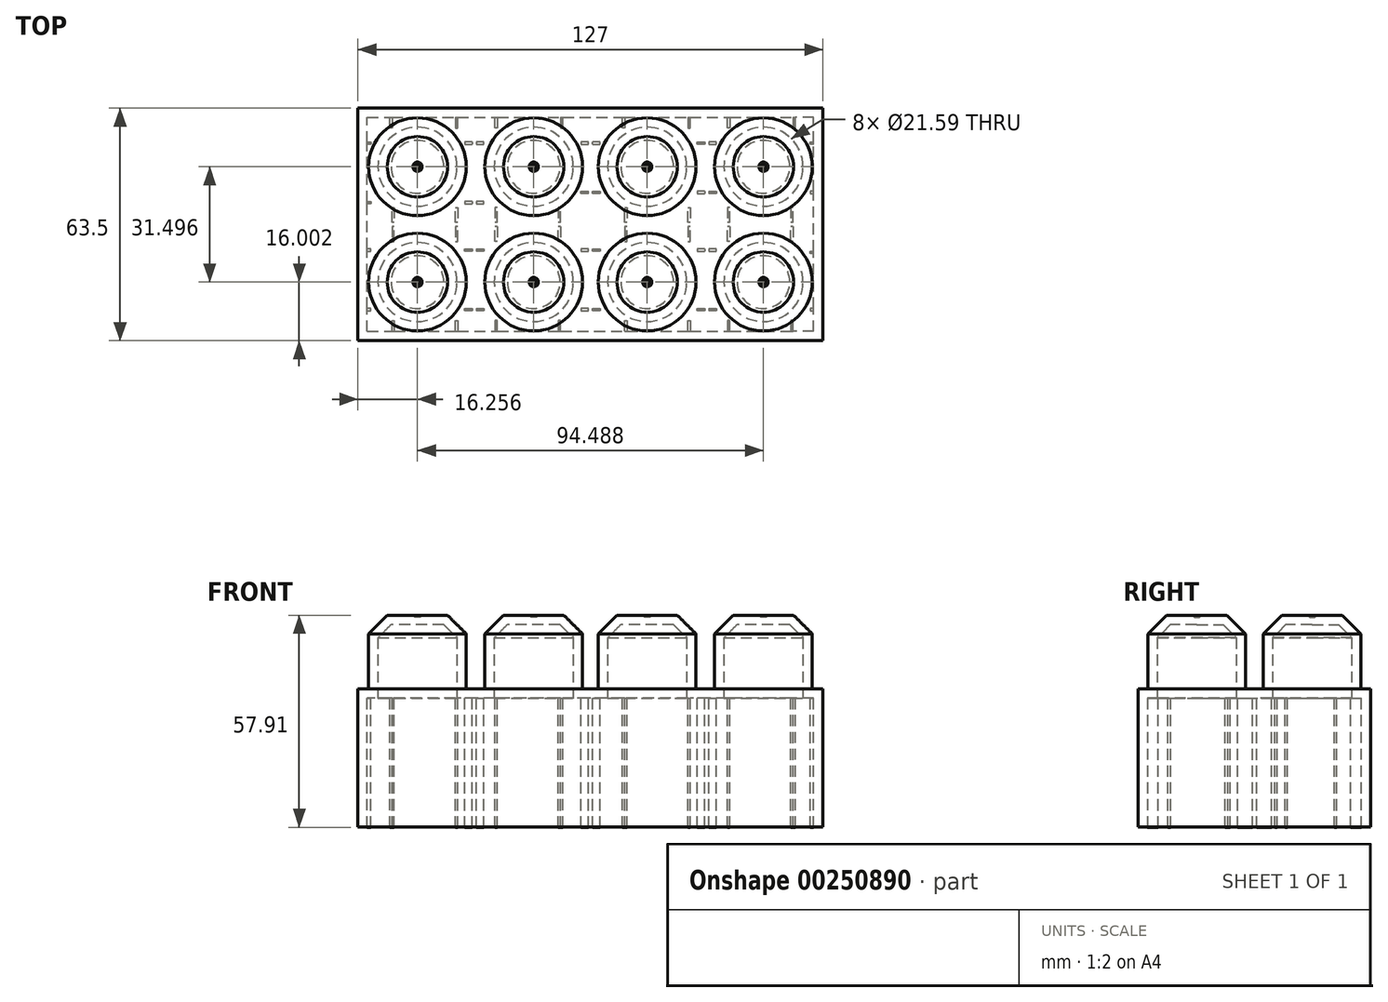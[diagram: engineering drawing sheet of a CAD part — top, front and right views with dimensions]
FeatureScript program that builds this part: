
annotation { "Feature Type Name" : "Feature", "Feature Type Description" : "" }
export const myFeature = defineFeature(function(context is Context, id is Id, definition is map)
    precondition{}
    {
        {
            var Q0;
            Q0=qCreatedBy(makeId("Front.planeOp"),FACE);
            var sketch = newSketch(context, id + "F0", { "sketchPlane" : qUnion([Q0])});
            skLineSegment(sketch, "E0", {"start": v(0, 0) * mm, "end": v(127, 0) * mm});
            skLineSegment(sketch, "E1", {"start": v(127, 0) * mm, "end": v(127, 37.74) * mm});
            skLineSegment(sketch, "E2", {"start": v(127, 37.74) * mm, "end": v(0, 37.74) * mm});
            skLineSegment(sketch, "E3", {"start": v(0, 37.74) * mm, "end": v(0, 0) * mm});
            skSolve(sketch);
        }
        {
            var Q0;
            Q0=makeQuery(id+"F0.imprint","IMPRINT",FACE,{"disambiguationData":[TD([[makeQuery(id+"F0.imprint","IMPRINT",EDGE,{"derivedFrom":sQuery(id+"F0.wireOp",EDGE,"E0")}),1.0]])]});
            extrude(context, id + "F1", {"entities" : qUnion([Q0]), "depth" : 63.5 * mm});
        }
        {
            var Q0;
            Q0=makeQuery(id+"F1.opExtrude","SWEPT_FACE",FACE,{"disambiguationData":[OSD([sQuery(id+"F0.wireOp",EDGE,"E2")])]});
            var sketch = newSketch(context, id + "F2", { "sketchPlane" : qUnion([Q0])});
            skLineSegment(sketch, "E4", {"start": v(0, -63.5) * mm, "end": v(16.26, -63.5) * mm});
            skLineSegment(sketch, "E5", {"start": v(16.26, -63.5) * mm, "end": v(16.26, -47.5) * mm});
            skCircle(sketch, "E6", {"center": v(16.26, -47.5) * mm, "radius": 13.34 * mm});
            skCircle(sketch, "E7", {"center": v(16.26, -16) * mm, "radius": 13.34 * mm});
            skLineSegment(sketch, "E8", {"start": v(0, -63.5) * mm, "end": v(48, -63.5) * mm});
            skCircle(sketch, "E9", {"center": v(48, -47.5) * mm, "radius": 13.34 * mm});
            skCircle(sketch, "E10", {"center": v(48, -16) * mm, "radius": 13.34 * mm});
            skCircle(sketch, "E11", {"center": v(110.74, -16) * mm, "radius": 13.34 * mm});
            skCircle(sketch, "E12", {"center": v(79, -16) * mm, "radius": 13.34 * mm});
            skCircle(sketch, "E13", {"center": v(79, -47.5) * mm, "radius": 13.34 * mm});
            skCircle(sketch, "E14", {"center": v(110.74, -47.5) * mm, "radius": 13.34 * mm});
            skSolve(sketch);
        }
        {
            var Q0;
            Q0 = qSketchRegion(id + "F2", true);
            extrude(context, id + "F3", {"entities" : qUnion([Q0]), "operationType" : NewBodyOperationType.ADD, "depth" : 20.1 * mm});
        }
        {
            var Q0;
            Q0=makeQuery(id+"F3.opExtrude","CAP_FACE",FACE,{"disambiguationData":[OSD([sQuery(id+"F2.wireOp",EDGE,"E6")])],"isStart":false});
            var Q1;
            Q1=makeQuery(id+"F3.opExtrude","CAP_EDGE",EDGE,{"disambiguationData":[OSD([sQuery(id+"F2.wireOp",EDGE,"E7")])],"isStart":false});
            var Q2;
            Q2=makeQuery(id+"F3.opExtrude","CAP_EDGE",EDGE,{"disambiguationData":[OSD([sQuery(id+"F2.wireOp",EDGE,"E10")])],"isStart":false});
            var Q3;
            Q3=makeQuery(id+"F3.opExtrude","CAP_FACE",FACE,{"disambiguationData":[OSD([sQuery(id+"F2.wireOp",EDGE,"E12")])],"isStart":false});
            var Q4;
            Q4=makeQuery(id+"F3.opExtrude","CAP_FACE",FACE,{"disambiguationData":[OSD([sQuery(id+"F2.wireOp",EDGE,"E9")])],"isStart":false});
            var Q5;
            Q5=makeQuery(id+"F3.opExtrude","CAP_FACE",FACE,{"disambiguationData":[OSD([sQuery(id+"F2.wireOp",EDGE,"E14")])],"isStart":false});
            var Q6;
            Q6=makeQuery(id+"F3.opExtrude","CAP_FACE",FACE,{"disambiguationData":[OSD([sQuery(id+"F2.wireOp",EDGE,"E11")])],"isStart":false});
            var Q7;
            Q7=makeQuery(id+"F3.opExtrude","CAP_FACE",FACE,{"disambiguationData":[OSD([sQuery(id+"F2.wireOp",EDGE,"E13")])],"isStart":false});
            chamfer(context, id + "F4", {"entities" : qUnion([Q0, Q1, Q2, Q3, Q4, Q5, Q6, Q7]), "width" : 5.08 * mm, "tangentPropagation" : true});
        }
        {
            var Q0;
            Q0=makeQuery(id+"F1.opExtrude","SWEPT_FACE",FACE,{"disambiguationData":[OSD([sQuery(id+"F0.wireOp",EDGE,"E0")])]});
            shell(context, id + "F5", {"entities" : qUnion([Q0]), "thickness" : 2.54 * mm});
        }
        {
            var Q0;
            Q0=makeQuery(id+"F5.opShell","OFFSET_FACE",FACE,{"disambiguationData":[OSD([sQuery(id+"F0.wireOp",EDGE,"E2")])]});
            var sketch = newSketch(context, id + "F6", { "sketchPlane" : qUnion([Q0])});
            skLineSegment(sketch, "E15.bottom", {"start": v(125.58, 62.08) * mm, "end": v(95.8, 62.08) * mm});
            skLineSegment(sketch, "E15.top", {"start": v(125.58, 1.42) * mm, "end": v(95.8, 1.42) * mm});
            skLineSegment(sketch, "E15.left", {"start": v(125.58, 62.08) * mm, "end": v(125.58, 32.3) * mm});
            skLineSegment(sketch, "E15.right", {"start": v(1.42, 62.08) * mm, "end": v(1.42, 32.3) * mm});
            skLineSegment(sketch, "E16", {"start": v(0, 0) * mm, "end": v(31.75, 0) * mm});
            skLineSegment(sketch, "E17", {"start": v(0, 0) * mm, "end": v(63.5, 0) * mm});
            skLineSegment(sketch, "E18", {"start": v(127, 0) * mm, "end": v(63.5, 0) * mm});
            skLineSegment(sketch, "E19", {"start": v(127, 0) * mm, "end": v(95.25, 0) * mm});
            skPoint(sketch, "E20.orphan", {"position": v(63.5, 63.5) * mm});
            skPoint(sketch, "E21.orphan", {"position": v(127, 31.75) * mm});
            skPoint(sketch, "E22.orphan", {"position": v(0, 31.75) * mm});
            skPoint(sketch, "E23", {"position": v(125.58, 32.3) * mm});
            skPoint(sketch, "E24", {"position": v(125.58, 31.2) * mm});
            skLineSegment(sketch, "E25", {"start": v(125.58, 32.3) * mm, "end": v(95.8, 32.3) * mm});
            skLineSegment(sketch, "E26", {"start": v(125.58, 31.2) * mm, "end": v(95.8, 31.2) * mm});
            skPoint(sketch, "E27", {"position": v(31.2, 1.42) * mm});
            skPoint(sketch, "E28", {"position": v(32.3, 1.42) * mm});
            skLineSegment(sketch, "E29", {"start": v(31.2, 1.42) * mm, "end": v(31.2, 31.2) * mm});
            skLineSegment(sketch, "E30", {"start": v(32.3, 1.42) * mm, "end": v(32.3, 31.2) * mm});
            skPoint(sketch, "E31", {"position": v(94.7, 1.42) * mm});
            skPoint(sketch, "E32", {"position": v(95.8, 1.42) * mm});
            skLineSegment(sketch, "E33", {"start": v(95.8, 1.42) * mm, "end": v(95.8, 31.2) * mm});
            skLineSegment(sketch, "E34", {"start": v(94.7, 1.42) * mm, "end": v(94.7, 31.2) * mm});
            skPoint(sketch, "E35", {"position": v(62.94, 62.08) * mm});
            skPoint(sketch, "E36", {"position": v(64.06, 62.08) * mm});
            skLineSegment(sketch, "E37", {"start": v(62.94, 62.08) * mm, "end": v(62.94, 32.3) * mm});
            skLineSegment(sketch, "E38", {"start": v(64.06, 62.08) * mm, "end": v(64.06, 32.3) * mm});
            skLineSegment(sketch, "E39.trimOffspring", {"start": v(31.2, 32.3) * mm, "end": v(1.42, 32.3) * mm});
            skLineSegment(sketch, "E40.trimOffspring", {"start": v(31.2, 32.3) * mm, "end": v(31.2, 62.08) * mm});
            skLineSegment(sketch, "E41.trimOffspring", {"start": v(32.3, 32.3) * mm, "end": v(32.3, 62.08) * mm});
            skLineSegment(sketch, "E42.trimOffspring", {"start": v(31.2, 31.2) * mm, "end": v(1.42, 31.2) * mm});
            skLineSegment(sketch, "E43.trimOffspring", {"start": v(62.94, 31.2) * mm, "end": v(62.94, 1.42) * mm});
            skLineSegment(sketch, "E44.trimOffspring", {"start": v(62.94, 32.3) * mm, "end": v(32.3, 32.3) * mm});
            skLineSegment(sketch, "E45.trimOffspring", {"start": v(64.06, 31.2) * mm, "end": v(64.06, 1.42) * mm});
            skLineSegment(sketch, "E46.trimOffspring", {"start": v(62.94, 31.2) * mm, "end": v(32.3, 31.2) * mm});
            skLineSegment(sketch, "E47.trimOffspring", {"start": v(94.7, 32.3) * mm, "end": v(94.7, 62.08) * mm});
            skLineSegment(sketch, "E48.trimOffspring", {"start": v(94.7, 32.3) * mm, "end": v(64.06, 32.3) * mm});
            skLineSegment(sketch, "E49.trimOffspring", {"start": v(95.8, 32.3) * mm, "end": v(95.8, 62.08) * mm});
            skLineSegment(sketch, "E50.trimOffspring", {"start": v(94.7, 31.2) * mm, "end": v(64.06, 31.2) * mm});
            skLineSegment(sketch, "E51.trimOffspring", {"start": v(62.94, 62.08) * mm, "end": v(32.3, 62.08) * mm});
            skLineSegment(sketch, "E52.trimOffspring", {"start": v(31.2, 62.08) * mm, "end": v(1.42, 62.08) * mm});
            skLineSegment(sketch, "E53.trimOffspring", {"start": v(1.42, 31.2) * mm, "end": v(1.42, 1.42) * mm});
            skLineSegment(sketch, "E54.trimOffspring", {"start": v(31.2, 1.42) * mm, "end": v(1.42, 1.42) * mm});
            skLineSegment(sketch, "E55.trimOffspring", {"start": v(62.94, 1.42) * mm, "end": v(32.3, 1.42) * mm});
            skLineSegment(sketch, "E56.trimOffspring", {"start": v(94.7, 1.42) * mm, "end": v(64.06, 1.42) * mm});
            skLineSegment(sketch, "E57.trimOffspring", {"start": v(125.58, 31.2) * mm, "end": v(125.58, 1.42) * mm});
            skLineSegment(sketch, "E58.trimOffspring", {"start": v(94.7, 62.08) * mm, "end": v(64.06, 62.08) * mm});
            skLineSegment(sketch, "E59", {"start": v(1.42, 31.2) * mm, "end": v(1.42, 32.3) * mm});
            skLineSegment(sketch, "E60", {"start": v(31.2, 1.42) * mm, "end": v(32.3, 1.42) * mm});
            skLineSegment(sketch, "E61", {"start": v(31.2, 62.08) * mm, "end": v(32.3, 62.08) * mm});
            skLineSegment(sketch, "E62", {"start": v(62.94, 62.08) * mm, "end": v(64.06, 62.08) * mm});
            skLineSegment(sketch, "E63", {"start": v(94.7, 62.08) * mm, "end": v(95.8, 62.08) * mm});
            skLineSegment(sketch, "E64", {"start": v(125.58, 32.3) * mm, "end": v(125.58, 31.2) * mm});
            skLineSegment(sketch, "E65", {"start": v(94.7, 1.42) * mm, "end": v(95.8, 1.42) * mm});
            skLineSegment(sketch, "E66", {"start": v(62.94, 1.42) * mm, "end": v(64.06, 1.42) * mm});
            skLineSegment(sketch, "E67", {"start": v(1.42, 1.42) * mm, "end": v(1.42, 9.3) * mm});
            skLineSegment(sketch, "E68", {"start": v(1.42, 9.3) * mm, "end": v(3.45, 9.3) * mm});
            skLineSegment(sketch, "E69", {"start": v(3.45, 9.3) * mm, "end": v(3.45, 9.93) * mm});
            skLineSegment(sketch, "E70", {"start": v(3.45, 9.93) * mm, "end": v(1.42, 9.93) * mm});
            skLineSegment(sketch, "E71", {"start": v(1.42, 1.42) * mm, "end": v(1.42, 25.55) * mm});
            skLineSegment(sketch, "E72", {"start": v(1.42, 25.55) * mm, "end": v(3.45, 25.55) * mm});
            skLineSegment(sketch, "E73", {"start": v(3.45, 25.55) * mm, "end": v(3.45, 26.19) * mm});
            skLineSegment(sketch, "E74", {"start": v(3.45, 26.19) * mm, "end": v(1.42, 26.19) * mm});
            skLineSegment(sketch, "E75.MirrorCS", {"start": v(3.45, 38.43) * mm, "end": v(1.42, 38.43) * mm});
            skLineSegment(sketch, "E76.MirrorCS", {"start": v(1.42, 39.07) * mm, "end": v(3.45, 39.07) * mm});
            skLineSegment(sketch, "E77.MirrorCS", {"start": v(3.45, 39.07) * mm, "end": v(3.45, 38.43) * mm});
            skLineSegment(sketch, "E78.MirrorCS", {"start": v(3.45, 54.69) * mm, "end": v(1.42, 54.69) * mm});
            skLineSegment(sketch, "E79.MirrorCS", {"start": v(1.42, 55.32) * mm, "end": v(3.45, 55.32) * mm});
            skLineSegment(sketch, "E80.MirrorCS", {"start": v(3.45, 55.32) * mm, "end": v(3.45, 54.69) * mm});
            skLineSegment(sketch, "E81", {"start": v(1.42, 1.42) * mm, "end": v(9.3, 1.42) * mm});
            skLineSegment(sketch, "E82", {"start": v(9.3, 1.42) * mm, "end": v(9.3, 5.49) * mm});
            skLineSegment(sketch, "E83", {"start": v(9.3, 5.49) * mm, "end": v(8.66, 5.49) * mm});
            skLineSegment(sketch, "E84", {"start": v(8.66, 5.49) * mm, "end": v(8.66, 1.42) * mm});
            skLineSegment(sketch, "E85", {"start": v(1.42, 1.42) * mm, "end": v(26.57, 1.42) * mm});
            skLineSegment(sketch, "E86", {"start": v(26.57, 1.42) * mm, "end": v(26.57, 5.49) * mm});
            skLineSegment(sketch, "E87", {"start": v(26.57, 5.49) * mm, "end": v(27.2, 5.49) * mm});
            skLineSegment(sketch, "E88", {"start": v(27.2, 5.49) * mm, "end": v(27.2, 1.42) * mm});
            skLineSegment(sketch, "E89", {"start": v(31.2, 1.42) * mm, "end": v(31.2, 9.3) * mm});
            skLineSegment(sketch, "E90", {"start": v(31.2, 9.3) * mm, "end": v(29.16, 9.3) * mm});
            skLineSegment(sketch, "E91", {"start": v(29.16, 9.3) * mm, "end": v(29.16, 9.93) * mm});
            skLineSegment(sketch, "E92", {"start": v(29.16, 9.93) * mm, "end": v(31.2, 9.93) * mm});
            skLineSegment(sketch, "E93", {"start": v(31.2, 1.42) * mm, "end": v(31.2, 25.55) * mm});
            skLineSegment(sketch, "E94", {"start": v(31.2, 25.55) * mm, "end": v(29.16, 25.55) * mm});
            skLineSegment(sketch, "E95", {"start": v(29.16, 25.55) * mm, "end": v(29.16, 26.19) * mm});
            skLineSegment(sketch, "E96", {"start": v(29.16, 26.19) * mm, "end": v(31.2, 26.19) * mm});
            skLineSegment(sketch, "E97", {"start": v(1.42, 31.2) * mm, "end": v(9.3, 31.2) * mm});
            skLineSegment(sketch, "E98", {"start": v(9.3, 31.2) * mm, "end": v(9.3, 27.13) * mm});
            skLineSegment(sketch, "E99", {"start": v(9.3, 27.13) * mm, "end": v(9.93, 27.13) * mm});
            skLineSegment(sketch, "E100", {"start": v(9.93, 27.13) * mm, "end": v(9.93, 31.2) * mm});
            skLineSegment(sketch, "E101", {"start": v(1.42, 31.2) * mm, "end": v(26.57, 31.2) * mm});
            skLineSegment(sketch, "E102", {"start": v(26.57, 31.2) * mm, "end": v(26.57, 27.13) * mm});
            skLineSegment(sketch, "E103", {"start": v(26.57, 27.13) * mm, "end": v(27.2, 27.13) * mm});
            skLineSegment(sketch, "E104", {"start": v(27.2, 27.13) * mm, "end": v(27.2, 31.2) * mm});
            skLineSegment(sketch, "E105.MirrorCS", {"start": v(29.16, 38.43) * mm, "end": v(31.2, 38.43) * mm});
            skLineSegment(sketch, "E106.MirrorCS", {"start": v(31.2, 39.07) * mm, "end": v(29.16, 39.07) * mm});
            skLineSegment(sketch, "E107.MirrorCS", {"start": v(29.16, 39.07) * mm, "end": v(29.16, 38.43) * mm});
            skLineSegment(sketch, "E108.MirrorCS", {"start": v(29.16, 54.69) * mm, "end": v(31.2, 54.69) * mm});
            skLineSegment(sketch, "E109.MirrorCS", {"start": v(31.2, 55.32) * mm, "end": v(29.16, 55.32) * mm});
            skLineSegment(sketch, "E110.MirrorCS", {"start": v(29.16, 55.32) * mm, "end": v(29.16, 54.69) * mm});
            skLineSegment(sketch, "E111", {"start": v(1.42, 62.08) * mm, "end": v(9.3, 62.08) * mm});
            skLineSegment(sketch, "E112", {"start": v(9.3, 62.08) * mm, "end": v(9.3, 58.01) * mm});
            skLineSegment(sketch, "E113", {"start": v(9.3, 58.01) * mm, "end": v(9.93, 58.01) * mm});
            skLineSegment(sketch, "E114", {"start": v(9.93, 58.01) * mm, "end": v(9.93, 62.08) * mm});
            skLineSegment(sketch, "E115", {"start": v(1.42, 62.08) * mm, "end": v(26.57, 62.08) * mm});
            skLineSegment(sketch, "E116", {"start": v(26.57, 62.08) * mm, "end": v(26.57, 58.01) * mm});
            skLineSegment(sketch, "E117", {"start": v(26.57, 58.01) * mm, "end": v(27.2, 58.01) * mm});
            skLineSegment(sketch, "E118", {"start": v(27.2, 58.01) * mm, "end": v(27.2, 62.08) * mm});
            skLineSegment(sketch, "E119", {"start": v(1.42, 32.3) * mm, "end": v(9.3, 32.3) * mm});
            skLineSegment(sketch, "E120", {"start": v(9.3, 32.3) * mm, "end": v(9.3, 36.37) * mm});
            skLineSegment(sketch, "E121", {"start": v(9.3, 36.37) * mm, "end": v(9.93, 36.37) * mm});
            skLineSegment(sketch, "E122", {"start": v(9.93, 36.37) * mm, "end": v(9.93, 32.3) * mm});
            skLineSegment(sketch, "E123", {"start": v(1.42, 32.3) * mm, "end": v(26.57, 32.3) * mm});
            skLineSegment(sketch, "E124", {"start": v(26.57, 32.3) * mm, "end": v(26.57, 36.37) * mm});
            skLineSegment(sketch, "E125", {"start": v(26.57, 36.37) * mm, "end": v(27.2, 36.37) * mm});
            skLineSegment(sketch, "E126", {"start": v(27.2, 36.37) * mm, "end": v(27.2, 32.3) * mm});
            skLineSegment(sketch, "E127.MirrorCS", {"start": v(37.41, 58.01) * mm, "end": v(37.41, 62.08) * mm});
            skLineSegment(sketch, "E128.MirrorCS", {"start": v(38.05, 62.08) * mm, "end": v(38.05, 58.01) * mm});
            skLineSegment(sketch, "E129.MirrorCS", {"start": v(55.32, 62.08) * mm, "end": v(55.32, 58.01) * mm});
            skLineSegment(sketch, "E130.MirrorCS", {"start": v(54.69, 58.01) * mm, "end": v(54.69, 62.08) * mm});
            skLineSegment(sketch, "E131.MirrorCS", {"start": v(55.32, 32.3) * mm, "end": v(55.32, 36.37) * mm});
            skLineSegment(sketch, "E132.MirrorCS", {"start": v(54.69, 36.37) * mm, "end": v(54.69, 32.3) * mm});
            skLineSegment(sketch, "E133.MirrorCS", {"start": v(38.05, 32.3) * mm, "end": v(38.05, 36.37) * mm});
            skLineSegment(sketch, "E134.MirrorCS", {"start": v(37.41, 36.37) * mm, "end": v(37.41, 32.3) * mm});
            skLineSegment(sketch, "E135.MirrorCS", {"start": v(38.05, 36.37) * mm, "end": v(37.41, 36.37) * mm});
            skLineSegment(sketch, "E136.MirrorCS", {"start": v(55.32, 36.37) * mm, "end": v(54.69, 36.37) * mm});
            skLineSegment(sketch, "E137.MirrorCS", {"start": v(55.32, 58.01) * mm, "end": v(54.69, 58.01) * mm});
            skLineSegment(sketch, "E138.MirrorCS", {"start": v(38.05, 58.01) * mm, "end": v(37.41, 58.01) * mm});
            skLineSegment(sketch, "E139", {"start": v(32.3, 32.3) * mm, "end": v(32.3, 38.43) * mm});
            skLineSegment(sketch, "E140", {"start": v(32.3, 38.43) * mm, "end": v(34.34, 38.43) * mm});
            skLineSegment(sketch, "E141", {"start": v(34.34, 38.43) * mm, "end": v(34.34, 39.07) * mm});
            skLineSegment(sketch, "E142", {"start": v(34.34, 39.07) * mm, "end": v(32.3, 39.07) * mm});
            skLineSegment(sketch, "E143", {"start": v(32.3, 54.69) * mm, "end": v(34.34, 54.69) * mm});
            skLineSegment(sketch, "E144", {"start": v(34.34, 54.69) * mm, "end": v(34.34, 55.32) * mm});
            skLineSegment(sketch, "E145", {"start": v(34.34, 55.32) * mm, "end": v(32.3, 55.32) * mm});
            skLineSegment(sketch, "E146.MirrorCS", {"start": v(37.41, 27.13) * mm, "end": v(37.41, 31.2) * mm});
            skLineSegment(sketch, "E147.MirrorCS", {"start": v(38.05, 31.2) * mm, "end": v(38.05, 27.13) * mm});
            skLineSegment(sketch, "E148.MirrorCS", {"start": v(38.05, 27.13) * mm, "end": v(37.41, 27.13) * mm});
            skLineSegment(sketch, "E149.MirrorCS", {"start": v(55.32, 31.2) * mm, "end": v(55.32, 27.13) * mm});
            skLineSegment(sketch, "E150.MirrorCS", {"start": v(54.69, 27.13) * mm, "end": v(54.69, 31.2) * mm});
            skLineSegment(sketch, "E151.MirrorCS", {"start": v(55.32, 27.13) * mm, "end": v(54.69, 27.13) * mm});
            skLineSegment(sketch, "E152.MirrorCS", {"start": v(55.96, 5.49) * mm, "end": v(55.96, 1.42) * mm});
            skLineSegment(sketch, "E153.MirrorCS", {"start": v(55.32, 1.42) * mm, "end": v(55.32, 5.49) * mm});
            skLineSegment(sketch, "E154.MirrorCS", {"start": v(55.32, 5.49) * mm, "end": v(55.96, 5.49) * mm});
            skLineSegment(sketch, "E155.MirrorCS", {"start": v(38.05, 5.49) * mm, "end": v(37.41, 5.49) * mm});
            skLineSegment(sketch, "E156.MirrorCS", {"start": v(38.05, 1.42) * mm, "end": v(38.05, 5.49) * mm});
            skLineSegment(sketch, "E157.MirrorCS", {"start": v(37.41, 5.49) * mm, "end": v(37.41, 1.42) * mm});
            skLineSegment(sketch, "E158.MirrorCS", {"start": v(73.43, 27.13) * mm, "end": v(73.43, 31.2) * mm});
            skLineSegment(sketch, "E159.MirrorCS", {"start": v(72.8, 31.2) * mm, "end": v(72.8, 27.13) * mm});
            skLineSegment(sketch, "E160.MirrorCS", {"start": v(72.8, 27.13) * mm, "end": v(73.43, 27.13) * mm});
            skLineSegment(sketch, "E161.MirrorCS", {"start": v(90.7, 27.13) * mm, "end": v(90.7, 31.2) * mm});
            skLineSegment(sketch, "E162.MirrorCS", {"start": v(90.07, 31.2) * mm, "end": v(90.07, 27.13) * mm});
            skLineSegment(sketch, "E163.MirrorCS", {"start": v(90.07, 27.13) * mm, "end": v(90.7, 27.13) * mm});
            skLineSegment(sketch, "E164.MirrorCS", {"start": v(90.7, 5.49) * mm, "end": v(90.7, 1.42) * mm});
            skLineSegment(sketch, "E165.MirrorCS", {"start": v(90.07, 1.42) * mm, "end": v(90.07, 5.49) * mm});
            skLineSegment(sketch, "E166.MirrorCS", {"start": v(90.07, 5.49) * mm, "end": v(90.7, 5.49) * mm});
            skLineSegment(sketch, "E167.MirrorCS", {"start": v(72.8, 1.42) * mm, "end": v(72.8, 5.49) * mm});
            skLineSegment(sketch, "E168.MirrorCS", {"start": v(72.16, 5.49) * mm, "end": v(72.16, 1.42) * mm});
            skLineSegment(sketch, "E169.MirrorCS", {"start": v(72.8, 5.49) * mm, "end": v(72.16, 5.49) * mm});
            skLineSegment(sketch, "E170.MirrorCS", {"start": v(118.82, 31.2) * mm, "end": v(118.82, 27.13) * mm});
            skLineSegment(sketch, "E171.MirrorCS", {"start": v(118.19, 27.13) * mm, "end": v(118.19, 31.2) * mm});
            skLineSegment(sketch, "E172.MirrorCS", {"start": v(118.82, 27.13) * mm, "end": v(118.19, 27.13) * mm});
            skLineSegment(sketch, "E173.MirrorCS", {"start": v(100.91, 27.13) * mm, "end": v(100.91, 31.2) * mm});
            skLineSegment(sketch, "E174.MirrorCS", {"start": v(101.55, 31.2) * mm, "end": v(101.55, 27.13) * mm});
            skLineSegment(sketch, "E175.MirrorCS", {"start": v(101.55, 27.13) * mm, "end": v(100.91, 27.13) * mm});
            skLineSegment(sketch, "E176.MirrorCS", {"start": v(101.55, 1.42) * mm, "end": v(101.55, 5.49) * mm});
            skLineSegment(sketch, "E177.MirrorCS", {"start": v(101.55, 5.49) * mm, "end": v(100.91, 5.49) * mm});
            skLineSegment(sketch, "E178.MirrorCS", {"start": v(100.91, 5.49) * mm, "end": v(100.91, 1.42) * mm});
            skLineSegment(sketch, "E179.MirrorCS", {"start": v(119.46, 5.49) * mm, "end": v(119.46, 1.42) * mm});
            skLineSegment(sketch, "E180.MirrorCS", {"start": v(118.82, 1.42) * mm, "end": v(118.82, 5.49) * mm});
            skLineSegment(sketch, "E181.MirrorCS", {"start": v(118.82, 5.49) * mm, "end": v(119.46, 5.49) * mm});
            skLineSegment(sketch, "E182.MirrorCS", {"start": v(90.07, 62.08) * mm, "end": v(90.07, 58.01) * mm});
            skLineSegment(sketch, "E183.MirrorCS", {"start": v(90.7, 58.01) * mm, "end": v(90.7, 62.08) * mm});
            skLineSegment(sketch, "E184.MirrorCS", {"start": v(90.07, 58.01) * mm, "end": v(90.7, 58.01) * mm});
            skLineSegment(sketch, "E185.MirrorCS", {"start": v(73.43, 58.01) * mm, "end": v(73.43, 62.08) * mm});
            skLineSegment(sketch, "E186.MirrorCS", {"start": v(72.8, 62.08) * mm, "end": v(72.8, 58.01) * mm});
            skLineSegment(sketch, "E187.MirrorCS", {"start": v(72.8, 58.01) * mm, "end": v(73.43, 58.01) * mm});
            skLineSegment(sketch, "E188.MirrorCS", {"start": v(73.43, 36.37) * mm, "end": v(73.43, 32.3) * mm});
            skLineSegment(sketch, "E189.MirrorCS", {"start": v(72.8, 36.37) * mm, "end": v(73.43, 36.37) * mm});
            skLineSegment(sketch, "E190.MirrorCS", {"start": v(72.8, 32.3) * mm, "end": v(72.8, 36.37) * mm});
            skLineSegment(sketch, "E191.MirrorCS", {"start": v(90.7, 36.37) * mm, "end": v(90.7, 32.3) * mm});
            skLineSegment(sketch, "E192.MirrorCS", {"start": v(90.07, 36.37) * mm, "end": v(90.7, 36.37) * mm});
            skLineSegment(sketch, "E193.MirrorCS", {"start": v(90.07, 32.3) * mm, "end": v(90.07, 36.37) * mm});
            skLineSegment(sketch, "E194.MirrorCS", {"start": v(100.91, 36.37) * mm, "end": v(100.91, 32.3) * mm});
            skLineSegment(sketch, "E195.MirrorCS", {"start": v(101.55, 32.3) * mm, "end": v(101.55, 36.37) * mm});
            skLineSegment(sketch, "E196.MirrorCS", {"start": v(101.55, 36.37) * mm, "end": v(100.91, 36.37) * mm});
            skLineSegment(sketch, "E197.MirrorCS", {"start": v(118.82, 32.3) * mm, "end": v(118.82, 36.37) * mm});
            skLineSegment(sketch, "E198.MirrorCS", {"start": v(118.19, 36.37) * mm, "end": v(118.19, 32.3) * mm});
            skLineSegment(sketch, "E199.MirrorCS", {"start": v(118.82, 36.37) * mm, "end": v(118.19, 36.37) * mm});
            skLineSegment(sketch, "E200.MirrorCS", {"start": v(101.55, 62.08) * mm, "end": v(101.55, 58.01) * mm});
            skLineSegment(sketch, "E201.MirrorCS", {"start": v(100.91, 58.01) * mm, "end": v(100.91, 62.08) * mm});
            skLineSegment(sketch, "E202.MirrorCS", {"start": v(101.55, 58.01) * mm, "end": v(100.91, 58.01) * mm});
            skLineSegment(sketch, "E203.MirrorCS", {"start": v(118.82, 62.08) * mm, "end": v(118.82, 58.01) * mm});
            skLineSegment(sketch, "E204.MirrorCS", {"start": v(118.19, 58.01) * mm, "end": v(118.19, 62.08) * mm});
            skLineSegment(sketch, "E205.MirrorCS", {"start": v(118.82, 58.01) * mm, "end": v(118.19, 58.01) * mm});
            skLineSegment(sketch, "E206", {"start": v(32.3, 26.19) * mm, "end": v(34.34, 26.19) * mm});
            skLineSegment(sketch, "E207", {"start": v(34.34, 26.19) * mm, "end": v(34.34, 25.55) * mm});
            skLineSegment(sketch, "E208", {"start": v(34.34, 25.55) * mm, "end": v(32.3, 25.55) * mm});
            skLineSegment(sketch, "E209", {"start": v(32.3, 9.93) * mm, "end": v(34.34, 9.93) * mm});
            skLineSegment(sketch, "E210", {"start": v(34.34, 9.93) * mm, "end": v(34.34, 9.3) * mm});
            skLineSegment(sketch, "E211", {"start": v(34.34, 9.3) * mm, "end": v(32.3, 9.3) * mm});
            skLineSegment(sketch, "E212", {"start": v(62.94, 1.42) * mm, "end": v(62.94, 9.3) * mm});
            skLineSegment(sketch, "E213", {"start": v(62.94, 9.3) * mm, "end": v(60.9, 9.3) * mm});
            skLineSegment(sketch, "E214", {"start": v(60.9, 9.3) * mm, "end": v(60.9, 9.93) * mm});
            skLineSegment(sketch, "E215", {"start": v(60.9, 9.93) * mm, "end": v(62.94, 9.93) * mm});
            skLineSegment(sketch, "E216", {"start": v(62.94, 54.69) * mm, "end": v(60.9, 54.69) * mm});
            skLineSegment(sketch, "E217", {"start": v(60.9, 54.69) * mm, "end": v(60.9, 55.32) * mm});
            skLineSegment(sketch, "E218", {"start": v(60.9, 55.32) * mm, "end": v(62.94, 55.32) * mm});
            skLineSegment(sketch, "E219", {"start": v(62.94, 38.43) * mm, "end": v(60.9, 38.43) * mm});
            skLineSegment(sketch, "E220", {"start": v(60.9, 38.43) * mm, "end": v(60.9, 39.07) * mm});
            skLineSegment(sketch, "E221", {"start": v(60.9, 39.07) * mm, "end": v(62.94, 39.07) * mm});
            skLineSegment(sketch, "E222", {"start": v(64.06, 38.43) * mm, "end": v(66.1, 38.43) * mm});
            skLineSegment(sketch, "E223", {"start": v(66.1, 38.43) * mm, "end": v(66.1, 39.07) * mm});
            skLineSegment(sketch, "E224", {"start": v(66.1, 39.07) * mm, "end": v(64.06, 39.07) * mm});
            skLineSegment(sketch, "E225", {"start": v(64.06, 54.69) * mm, "end": v(66.1, 54.69) * mm});
            skLineSegment(sketch, "E226", {"start": v(66.1, 54.69) * mm, "end": v(66.1, 55.32) * mm});
            skLineSegment(sketch, "E227", {"start": v(66.1, 55.32) * mm, "end": v(64.06, 55.32) * mm});
            skLineSegment(sketch, "E228", {"start": v(94.7, 55.32) * mm, "end": v(92.66, 55.32) * mm});
            skLineSegment(sketch, "E229", {"start": v(92.66, 55.32) * mm, "end": v(92.66, 54.69) * mm});
            skLineSegment(sketch, "E230", {"start": v(92.66, 54.69) * mm, "end": v(94.7, 54.69) * mm});
            skLineSegment(sketch, "E231", {"start": v(94.7, 38.43) * mm, "end": v(92.66, 38.43) * mm});
            skLineSegment(sketch, "E232", {"start": v(92.66, 38.43) * mm, "end": v(92.66, 39.07) * mm});
            skLineSegment(sketch, "E233", {"start": v(92.66, 39.07) * mm, "end": v(94.7, 39.07) * mm});
            skLineSegment(sketch, "E234.MirrorCS", {"start": v(60.9, 22.68) * mm, "end": v(62.94, 22.68) * mm});
            skLineSegment(sketch, "E235.MirrorCS", {"start": v(62.94, 23.32) * mm, "end": v(60.9, 23.32) * mm});
            skLineSegment(sketch, "E236.MirrorCS", {"start": v(60.9, 23.32) * mm, "end": v(60.9, 22.68) * mm});
            skLineSegment(sketch, "E237", {"start": v(64.06, 22.68) * mm, "end": v(66.1, 22.68) * mm});
            skLineSegment(sketch, "E238", {"start": v(66.1, 22.68) * mm, "end": v(66.1, 23.32) * mm});
            skLineSegment(sketch, "E239", {"start": v(66.1, 23.32) * mm, "end": v(64.06, 23.32) * mm});
            skLineSegment(sketch, "E240.MirrorCS", {"start": v(64.06, 9.93) * mm, "end": v(66.1, 9.93) * mm});
            skLineSegment(sketch, "E241.MirrorCS", {"start": v(66.1, 9.3) * mm, "end": v(64.06, 9.3) * mm});
            skLineSegment(sketch, "E242.MirrorCS", {"start": v(66.1, 9.93) * mm, "end": v(66.1, 9.3) * mm});
            skLineSegment(sketch, "E243.MirrorCS", {"start": v(92.66, 23.32) * mm, "end": v(94.7, 23.32) * mm});
            skLineSegment(sketch, "E244.MirrorCS", {"start": v(94.7, 22.68) * mm, "end": v(92.66, 22.68) * mm});
            skLineSegment(sketch, "E245.MirrorCS", {"start": v(92.66, 22.68) * mm, "end": v(92.66, 23.32) * mm});
            skLineSegment(sketch, "E246.MirrorCS", {"start": v(94.7, 9.93) * mm, "end": v(92.66, 9.93) * mm});
            skLineSegment(sketch, "E247.MirrorCS", {"start": v(92.66, 9.3) * mm, "end": v(94.7, 9.3) * mm});
            skLineSegment(sketch, "E248.MirrorCS", {"start": v(92.66, 9.93) * mm, "end": v(92.66, 9.3) * mm});
            skLineSegment(sketch, "E249", {"start": v(95.8, 22.68) * mm, "end": v(97.84, 22.68) * mm});
            skLineSegment(sketch, "E250", {"start": v(97.84, 22.68) * mm, "end": v(97.84, 23.32) * mm});
            skLineSegment(sketch, "E251", {"start": v(97.84, 23.32) * mm, "end": v(95.8, 23.32) * mm});
            skLineSegment(sketch, "E252.MirrorCS", {"start": v(123.55, 23.32) * mm, "end": v(125.58, 23.32) * mm});
            skLineSegment(sketch, "E253.MirrorCS", {"start": v(125.58, 22.68) * mm, "end": v(123.55, 22.68) * mm});
            skLineSegment(sketch, "E254.MirrorCS", {"start": v(123.55, 22.68) * mm, "end": v(123.55, 23.32) * mm});
            skLineSegment(sketch, "E255.MirrorCS", {"start": v(95.8, 9.93) * mm, "end": v(97.84, 9.93) * mm});
            skLineSegment(sketch, "E256.MirrorCS", {"start": v(97.84, 9.3) * mm, "end": v(95.8, 9.3) * mm});
            skLineSegment(sketch, "E257.MirrorCS", {"start": v(97.84, 9.93) * mm, "end": v(97.84, 9.3) * mm});
            skLineSegment(sketch, "E258.MirrorCS", {"start": v(123.55, 9.3) * mm, "end": v(125.58, 9.3) * mm});
            skLineSegment(sketch, "E259.MirrorCS", {"start": v(125.58, 9.93) * mm, "end": v(123.55, 9.93) * mm});
            skLineSegment(sketch, "E260.MirrorCS", {"start": v(123.55, 9.93) * mm, "end": v(123.55, 9.3) * mm});
            skLineSegment(sketch, "E261", {"start": v(95.8, 54.69) * mm, "end": v(97.84, 54.69) * mm});
            skLineSegment(sketch, "E262", {"start": v(97.84, 54.69) * mm, "end": v(97.84, 55.32) * mm});
            skLineSegment(sketch, "E263", {"start": v(97.84, 55.32) * mm, "end": v(95.8, 55.32) * mm});
            skLineSegment(sketch, "E264.MirrorCS", {"start": v(123.55, 55.32) * mm, "end": v(125.58, 55.32) * mm});
            skLineSegment(sketch, "E265.MirrorCS", {"start": v(125.58, 54.69) * mm, "end": v(123.55, 54.69) * mm});
            skLineSegment(sketch, "E266.MirrorCS", {"start": v(123.55, 54.69) * mm, "end": v(123.55, 55.32) * mm});
            skLineSegment(sketch, "E267.MirrorCS", {"start": v(125.58, 39.7) * mm, "end": v(123.55, 39.7) * mm});
            skLineSegment(sketch, "E268.MirrorCS", {"start": v(123.55, 39.07) * mm, "end": v(125.58, 39.07) * mm});
            skLineSegment(sketch, "E269.MirrorCS", {"start": v(123.55, 39.7) * mm, "end": v(123.55, 39.07) * mm});
            skLineSegment(sketch, "E270", {"start": v(95.8, 39.07) * mm, "end": v(97.84, 39.07) * mm});
            skLineSegment(sketch, "E271", {"start": v(97.84, 39.07) * mm, "end": v(97.84, 38.43) * mm});
            skLineSegment(sketch, "E272", {"start": v(97.84, 38.43) * mm, "end": v(95.8, 38.43) * mm});
            skSolve(sketch);
        }
        {
            var Q0;
            {var subQ52=sQuery(id+"F6.wireOp",EDGE,"E139");Q0=makeQuery(id+"F6.imprint","IMPRINT",FACE,{"disambiguationData":[TD([[makeQuery(id+"F6.imprint","IMPRINT",EDGE,{"derivedFrom":subQ52}),1.0]])]});}
            var Q1;
            {var subQ0=sQuery(id+"F6.wireOp",EDGE,"E77.MirrorCS");Q1=makeQuery(id+"F6.imprint","IMPRINT",FACE,{"disambiguationData":[TD([[makeQuery(id+"F6.imprint","IMPRINT",EDGE,{"derivedFrom":subQ0}),-1.0]])]});}
            var Q2;
            {var subQ0=sQuery(id+"F6.wireOp",EDGE,"E120");Q2=makeQuery(id+"F6.imprint","IMPRINT",FACE,{"disambiguationData":[TD([[makeQuery(id+"F6.imprint","IMPRINT",EDGE,{"derivedFrom":subQ0}),-1.0]])]});}
            var Q3;
            {var subQ0=sQuery(id+"F6.wireOp",EDGE,"E124");Q3=makeQuery(id+"F6.imprint","IMPRINT",FACE,{"disambiguationData":[TD([[makeQuery(id+"F6.imprint","IMPRINT",EDGE,{"derivedFrom":subQ0}),-1.0]])]});}
            var Q4;
            {var subQ0=sQuery(id+"F6.wireOp",EDGE,"E105.MirrorCS");Q4=makeQuery(id+"F6.imprint","IMPRINT",FACE,{"disambiguationData":[TD([[makeQuery(id+"F6.imprint","IMPRINT",EDGE,{"derivedFrom":subQ0}),1.0]])]});}
            var Q5;
            {var subQ0=sQuery(id+"F6.wireOp",EDGE,"E80.MirrorCS");Q5=makeQuery(id+"F6.imprint","IMPRINT",FACE,{"disambiguationData":[TD([[makeQuery(id+"F6.imprint","IMPRINT",EDGE,{"derivedFrom":subQ0}),-1.0]])]});}
            var Q6;
            {var subQ0=sQuery(id+"F6.wireOp",EDGE,"E113");Q6=makeQuery(id+"F6.imprint","IMPRINT",FACE,{"disambiguationData":[TD([[makeQuery(id+"F6.imprint","IMPRINT",EDGE,{"derivedFrom":subQ0}),1.0]])]});}
            var Q7;
            {var subQ0=sQuery(id+"F6.wireOp",EDGE,"E117");Q7=makeQuery(id+"F6.imprint","IMPRINT",FACE,{"disambiguationData":[TD([[makeQuery(id+"F6.imprint","IMPRINT",EDGE,{"derivedFrom":subQ0}),1.0]])]});}
            var Q8;
            {var subQ0=sQuery(id+"F6.wireOp",EDGE,"E108.MirrorCS");Q8=makeQuery(id+"F6.imprint","IMPRINT",FACE,{"disambiguationData":[TD([[makeQuery(id+"F6.imprint","IMPRINT",EDGE,{"derivedFrom":subQ0}),1.0]])]});}
            var Q9;
            {var subQ0=sQuery(id+"F6.wireOp",EDGE,"E98");Q9=makeQuery(id+"F6.imprint","IMPRINT",FACE,{"disambiguationData":[TD([[makeQuery(id+"F6.imprint","IMPRINT",EDGE,{"derivedFrom":subQ0}),1.0]])]});}
            var Q10;
            {var subQ0=sQuery(id+"F6.wireOp",EDGE,"E73");Q10=makeQuery(id+"F6.imprint","IMPRINT",FACE,{"disambiguationData":[TD([[makeQuery(id+"F6.imprint","IMPRINT",EDGE,{"derivedFrom":subQ0}),1.0]])]});}
            var Q11;
            {var subQ0=sQuery(id+"F6.wireOp",EDGE,"E102");Q11=makeQuery(id+"F6.imprint","IMPRINT",FACE,{"disambiguationData":[TD([[makeQuery(id+"F6.imprint","IMPRINT",EDGE,{"derivedFrom":subQ0}),1.0]])]});}
            var Q12;
            {var subQ0=sQuery(id+"F6.wireOp",EDGE,"E94");Q12=makeQuery(id+"F6.imprint","IMPRINT",FACE,{"disambiguationData":[TD([[makeQuery(id+"F6.imprint","IMPRINT",EDGE,{"derivedFrom":subQ0}),-1.0]])]});}
            var Q13;
            {var subQ0=sQuery(id+"F6.wireOp",EDGE,"E69");Q13=makeQuery(id+"F6.imprint","IMPRINT",FACE,{"disambiguationData":[TD([[makeQuery(id+"F6.imprint","IMPRINT",EDGE,{"derivedFrom":subQ0}),1.0]])]});}
            var Q14;
            {var subQ0=sQuery(id+"F6.wireOp",EDGE,"E83");Q14=makeQuery(id+"F6.imprint","IMPRINT",FACE,{"disambiguationData":[TD([[makeQuery(id+"F6.imprint","IMPRINT",EDGE,{"derivedFrom":subQ0}),1.0]])]});}
            var Q15;
            {var subQ0=sQuery(id+"F6.wireOp",EDGE,"E87");Q15=makeQuery(id+"F6.imprint","IMPRINT",FACE,{"disambiguationData":[TD([[makeQuery(id+"F6.imprint","IMPRINT",EDGE,{"derivedFrom":subQ0}),-1.0]])]});}
            var Q16;
            {var subQ0=sQuery(id+"F6.wireOp",EDGE,"E90");Q16=makeQuery(id+"F6.imprint","IMPRINT",FACE,{"disambiguationData":[TD([[makeQuery(id+"F6.imprint","IMPRINT",EDGE,{"derivedFrom":subQ0}),-1.0]])]});}
            var Q17;
            {var subQ0=sQuery(id+"F6.wireOp",EDGE,"E209");Q17=makeQuery(id+"F6.imprint","IMPRINT",FACE,{"disambiguationData":[TD([[makeQuery(id+"F6.imprint","IMPRINT",EDGE,{"derivedFrom":subQ0}),-1.0]])]});}
            var Q18;
            {var subQ0=sQuery(id+"F6.wireOp",EDGE,"E155.MirrorCS");Q18=makeQuery(id+"F6.imprint","IMPRINT",FACE,{"disambiguationData":[TD([[makeQuery(id+"F6.imprint","IMPRINT",EDGE,{"derivedFrom":subQ0}),1.0]])]});}
            var Q19;
            {var subQ0=sQuery(id+"F6.wireOp",EDGE,"E146.MirrorCS");Q19=makeQuery(id+"F6.imprint","IMPRINT",FACE,{"disambiguationData":[TD([[makeQuery(id+"F6.imprint","IMPRINT",EDGE,{"derivedFrom":subQ0}),-1.0]])]});}
            var Q20;
            {var subQ0=sQuery(id+"F6.wireOp",EDGE,"E206");Q20=makeQuery(id+"F6.imprint","IMPRINT",FACE,{"disambiguationData":[TD([[makeQuery(id+"F6.imprint","IMPRINT",EDGE,{"derivedFrom":subQ0}),-1.0]])]});}
            var Q21;
            {var subQ0=sQuery(id+"F6.wireOp",EDGE,"E149.MirrorCS");Q21=makeQuery(id+"F6.imprint","IMPRINT",FACE,{"disambiguationData":[TD([[makeQuery(id+"F6.imprint","IMPRINT",EDGE,{"derivedFrom":subQ0}),-1.0]])]});}
            var Q22;
            {var subQ0=sQuery(id+"F6.wireOp",EDGE,"E154.MirrorCS");Q22=makeQuery(id+"F6.imprint","IMPRINT",FACE,{"disambiguationData":[TD([[makeQuery(id+"F6.imprint","IMPRINT",EDGE,{"derivedFrom":subQ0}),-1.0]])]});}
            var Q23;
            {var subQ0=sQuery(id+"F6.wireOp",EDGE,"E213");Q23=makeQuery(id+"F6.imprint","IMPRINT",FACE,{"disambiguationData":[TD([[makeQuery(id+"F6.imprint","IMPRINT",EDGE,{"derivedFrom":subQ0}),-1.0]])]});}
            var Q24;
            {var subQ0=sQuery(id+"F6.wireOp",EDGE,"E234.MirrorCS");Q24=makeQuery(id+"F6.imprint","IMPRINT",FACE,{"disambiguationData":[TD([[makeQuery(id+"F6.imprint","IMPRINT",EDGE,{"derivedFrom":subQ0}),1.0]])]});}
            var Q25;
            {var subQ0=sQuery(id+"F6.wireOp",EDGE,"E237");Q25=makeQuery(id+"F6.imprint","IMPRINT",FACE,{"disambiguationData":[TD([[makeQuery(id+"F6.imprint","IMPRINT",EDGE,{"derivedFrom":subQ0}),1.0]])]});}
            var Q26;
            {var subQ0=sQuery(id+"F6.wireOp",EDGE,"E240.MirrorCS");Q26=makeQuery(id+"F6.imprint","IMPRINT",FACE,{"disambiguationData":[TD([[makeQuery(id+"F6.imprint","IMPRINT",EDGE,{"derivedFrom":subQ0}),-1.0]])]});}
            var Q27;
            {var subQ0=sQuery(id+"F6.wireOp",EDGE,"E169.MirrorCS");Q27=makeQuery(id+"F6.imprint","IMPRINT",FACE,{"disambiguationData":[TD([[makeQuery(id+"F6.imprint","IMPRINT",EDGE,{"derivedFrom":subQ0}),1.0]])]});}
            var Q28;
            {var subQ0=sQuery(id+"F6.wireOp",EDGE,"E158.MirrorCS");Q28=makeQuery(id+"F6.imprint","IMPRINT",FACE,{"disambiguationData":[TD([[makeQuery(id+"F6.imprint","IMPRINT",EDGE,{"derivedFrom":subQ0}),1.0]])]});}
            var Q29;
            {var subQ0=sQuery(id+"F6.wireOp",EDGE,"E161.MirrorCS");Q29=makeQuery(id+"F6.imprint","IMPRINT",FACE,{"disambiguationData":[TD([[makeQuery(id+"F6.imprint","IMPRINT",EDGE,{"derivedFrom":subQ0}),1.0]])]});}
            var Q30;
            {var subQ0=sQuery(id+"F6.wireOp",EDGE,"E243.MirrorCS");Q30=makeQuery(id+"F6.imprint","IMPRINT",FACE,{"disambiguationData":[TD([[makeQuery(id+"F6.imprint","IMPRINT",EDGE,{"derivedFrom":subQ0}),-1.0]])]});}
            var Q31;
            {var subQ0=sQuery(id+"F6.wireOp",EDGE,"E246.MirrorCS");Q31=makeQuery(id+"F6.imprint","IMPRINT",FACE,{"disambiguationData":[TD([[makeQuery(id+"F6.imprint","IMPRINT",EDGE,{"derivedFrom":subQ0}),1.0]])]});}
            var Q32;
            {var subQ0=sQuery(id+"F6.wireOp",EDGE,"E166.MirrorCS");Q32=makeQuery(id+"F6.imprint","IMPRINT",FACE,{"disambiguationData":[TD([[makeQuery(id+"F6.imprint","IMPRINT",EDGE,{"derivedFrom":subQ0}),-1.0]])]});}
            var Q33;
            {var subQ0=sQuery(id+"F6.wireOp",EDGE,"E249");Q33=makeQuery(id+"F6.imprint","IMPRINT",FACE,{"disambiguationData":[TD([[makeQuery(id+"F6.imprint","IMPRINT",EDGE,{"derivedFrom":subQ0}),1.0]])]});}
            var Q34;
            {var subQ0=sQuery(id+"F6.wireOp",EDGE,"E173.MirrorCS");Q34=makeQuery(id+"F6.imprint","IMPRINT",FACE,{"disambiguationData":[TD([[makeQuery(id+"F6.imprint","IMPRINT",EDGE,{"derivedFrom":subQ0}),-1.0]])]});}
            var Q35;
            {var subQ0=sQuery(id+"F6.wireOp",EDGE,"E170.MirrorCS");Q35=makeQuery(id+"F6.imprint","IMPRINT",FACE,{"disambiguationData":[TD([[makeQuery(id+"F6.imprint","IMPRINT",EDGE,{"derivedFrom":subQ0}),-1.0]])]});}
            var Q36;
            {var subQ0=sQuery(id+"F6.wireOp",EDGE,"E255.MirrorCS");Q36=makeQuery(id+"F6.imprint","IMPRINT",FACE,{"disambiguationData":[TD([[makeQuery(id+"F6.imprint","IMPRINT",EDGE,{"derivedFrom":subQ0}),-1.0]])]});}
            var Q37;
            {var subQ0=sQuery(id+"F6.wireOp",EDGE,"E177.MirrorCS");Q37=makeQuery(id+"F6.imprint","IMPRINT",FACE,{"disambiguationData":[TD([[makeQuery(id+"F6.imprint","IMPRINT",EDGE,{"derivedFrom":subQ0}),1.0]])]});}
            var Q38;
            {var subQ0=sQuery(id+"F6.wireOp",EDGE,"E181.MirrorCS");Q38=makeQuery(id+"F6.imprint","IMPRINT",FACE,{"disambiguationData":[TD([[makeQuery(id+"F6.imprint","IMPRINT",EDGE,{"derivedFrom":subQ0}),-1.0]])]});}
            var Q39;
            {var subQ0=sQuery(id+"F6.wireOp",EDGE,"E260.MirrorCS");Q39=makeQuery(id+"F6.imprint","IMPRINT",FACE,{"disambiguationData":[TD([[makeQuery(id+"F6.imprint","IMPRINT",EDGE,{"derivedFrom":subQ0}),1.0]])]});}
            var Q40;
            {var subQ0=sQuery(id+"F6.wireOp",EDGE,"E254.MirrorCS");Q40=makeQuery(id+"F6.imprint","IMPRINT",FACE,{"disambiguationData":[TD([[makeQuery(id+"F6.imprint","IMPRINT",EDGE,{"derivedFrom":subQ0}),-1.0]])]});}
            var Q41;
            {var subQ0=sQuery(id+"F6.wireOp",EDGE,"E194.MirrorCS");Q41=makeQuery(id+"F6.imprint","IMPRINT",FACE,{"disambiguationData":[TD([[makeQuery(id+"F6.imprint","IMPRINT",EDGE,{"derivedFrom":subQ0}),1.0]])]});}
            var Q42;
            {var subQ0=sQuery(id+"F6.wireOp",EDGE,"E270");Q42=makeQuery(id+"F6.imprint","IMPRINT",FACE,{"disambiguationData":[TD([[makeQuery(id+"F6.imprint","IMPRINT",EDGE,{"derivedFrom":subQ0}),-1.0]])]});}
            var Q43;
            {var subQ0=sQuery(id+"F6.wireOp",EDGE,"E197.MirrorCS");Q43=makeQuery(id+"F6.imprint","IMPRINT",FACE,{"disambiguationData":[TD([[makeQuery(id+"F6.imprint","IMPRINT",EDGE,{"derivedFrom":subQ0}),1.0]])]});}
            var Q44;
            {var subQ0=sQuery(id+"F6.wireOp",EDGE,"E269.MirrorCS");Q44=makeQuery(id+"F6.imprint","IMPRINT",FACE,{"disambiguationData":[TD([[makeQuery(id+"F6.imprint","IMPRINT",EDGE,{"derivedFrom":subQ0}),1.0]])]});}
            var Q45;
            {var subQ0=sQuery(id+"F6.wireOp",EDGE,"E266.MirrorCS");Q45=makeQuery(id+"F6.imprint","IMPRINT",FACE,{"disambiguationData":[TD([[makeQuery(id+"F6.imprint","IMPRINT",EDGE,{"derivedFrom":subQ0}),-1.0]])]});}
            var Q46;
            {var subQ0=sQuery(id+"F6.wireOp",EDGE,"E261");Q46=makeQuery(id+"F6.imprint","IMPRINT",FACE,{"disambiguationData":[TD([[makeQuery(id+"F6.imprint","IMPRINT",EDGE,{"derivedFrom":subQ0}),1.0]])]});}
            var Q47;
            {var subQ0=sQuery(id+"F6.wireOp",EDGE,"E202.MirrorCS");Q47=makeQuery(id+"F6.imprint","IMPRINT",FACE,{"disambiguationData":[TD([[makeQuery(id+"F6.imprint","IMPRINT",EDGE,{"derivedFrom":subQ0}),-1.0]])]});}
            var Q48;
            {var subQ0=sQuery(id+"F6.wireOp",EDGE,"E205.MirrorCS");Q48=makeQuery(id+"F6.imprint","IMPRINT",FACE,{"disambiguationData":[TD([[makeQuery(id+"F6.imprint","IMPRINT",EDGE,{"derivedFrom":subQ0}),-1.0]])]});}
            var Q49;
            {var subQ0=sQuery(id+"F6.wireOp",EDGE,"E184.MirrorCS");Q49=makeQuery(id+"F6.imprint","IMPRINT",FACE,{"disambiguationData":[TD([[makeQuery(id+"F6.imprint","IMPRINT",EDGE,{"derivedFrom":subQ0}),1.0]])]});}
            var Q50;
            {var subQ0=sQuery(id+"F6.wireOp",EDGE,"E228");Q50=makeQuery(id+"F6.imprint","IMPRINT",FACE,{"disambiguationData":[TD([[makeQuery(id+"F6.imprint","IMPRINT",EDGE,{"derivedFrom":subQ0}),1.0]])]});}
            var Q51;
            {var subQ0=sQuery(id+"F6.wireOp",EDGE,"E231");Q51=makeQuery(id+"F6.imprint","IMPRINT",FACE,{"disambiguationData":[TD([[makeQuery(id+"F6.imprint","IMPRINT",EDGE,{"derivedFrom":subQ0}),-1.0]])]});}
            var Q52;
            {var subQ0=sQuery(id+"F6.wireOp",EDGE,"E191.MirrorCS");Q52=makeQuery(id+"F6.imprint","IMPRINT",FACE,{"disambiguationData":[TD([[makeQuery(id+"F6.imprint","IMPRINT",EDGE,{"derivedFrom":subQ0}),-1.0]])]});}
            var Q53;
            {var subQ0=sQuery(id+"F6.wireOp",EDGE,"E188.MirrorCS");Q53=makeQuery(id+"F6.imprint","IMPRINT",FACE,{"disambiguationData":[TD([[makeQuery(id+"F6.imprint","IMPRINT",EDGE,{"derivedFrom":subQ0}),-1.0]])]});}
            var Q54;
            {var subQ0=sQuery(id+"F6.wireOp",EDGE,"E187.MirrorCS");Q54=makeQuery(id+"F6.imprint","IMPRINT",FACE,{"disambiguationData":[TD([[makeQuery(id+"F6.imprint","IMPRINT",EDGE,{"derivedFrom":subQ0}),1.0]])]});}
            var Q55;
            {var subQ0=sQuery(id+"F6.wireOp",EDGE,"E216");Q55=makeQuery(id+"F6.imprint","IMPRINT",FACE,{"disambiguationData":[TD([[makeQuery(id+"F6.imprint","IMPRINT",EDGE,{"derivedFrom":subQ0}),-1.0]])]});}
            var Q56;
            {var subQ0=sQuery(id+"F6.wireOp",EDGE,"E219");Q56=makeQuery(id+"F6.imprint","IMPRINT",FACE,{"disambiguationData":[TD([[makeQuery(id+"F6.imprint","IMPRINT",EDGE,{"derivedFrom":subQ0}),-1.0]])]});}
            var Q57;
            {var subQ0=sQuery(id+"F6.wireOp",EDGE,"E131.MirrorCS");Q57=makeQuery(id+"F6.imprint","IMPRINT",FACE,{"disambiguationData":[TD([[makeQuery(id+"F6.imprint","IMPRINT",EDGE,{"derivedFrom":subQ0}),1.0]])]});}
            var Q58;
            {var subQ0=sQuery(id+"F6.wireOp",EDGE,"E137.MirrorCS");Q58=makeQuery(id+"F6.imprint","IMPRINT",FACE,{"disambiguationData":[TD([[makeQuery(id+"F6.imprint","IMPRINT",EDGE,{"derivedFrom":subQ0}),-1.0]])]});}
            var Q59;
            {var subQ0=sQuery(id+"F6.wireOp",EDGE,"E222");Q59=makeQuery(id+"F6.imprint","IMPRINT",FACE,{"disambiguationData":[TD([[makeQuery(id+"F6.imprint","IMPRINT",EDGE,{"derivedFrom":subQ0}),1.0]])]});}
            var Q60;
            {var subQ0=sQuery(id+"F6.wireOp",EDGE,"E225");Q60=makeQuery(id+"F6.imprint","IMPRINT",FACE,{"disambiguationData":[TD([[makeQuery(id+"F6.imprint","IMPRINT",EDGE,{"derivedFrom":subQ0}),1.0]])]});}
            var Q61;
            {var subQ0=sQuery(id+"F6.wireOp",EDGE,"E143");Q61=makeQuery(id+"F6.imprint","IMPRINT",FACE,{"disambiguationData":[TD([[makeQuery(id+"F6.imprint","IMPRINT",EDGE,{"derivedFrom":subQ0}),1.0]])]});}
            var Q62;
            {var subQ0=sQuery(id+"F6.wireOp",EDGE,"E138.MirrorCS");Q62=makeQuery(id+"F6.imprint","IMPRINT",FACE,{"disambiguationData":[TD([[makeQuery(id+"F6.imprint","IMPRINT",EDGE,{"derivedFrom":subQ0}),-1.0]])]});}
            var Q63;
            {var subQ0=sQuery(id+"F6.wireOp",EDGE,"E140");Q63=makeQuery(id+"F6.imprint","IMPRINT",FACE,{"disambiguationData":[TD([[makeQuery(id+"F6.imprint","IMPRINT",EDGE,{"derivedFrom":subQ0}),1.0]])]});}
            var Q64;
            {var subQ0=sQuery(id+"F6.wireOp",EDGE,"E133.MirrorCS");Q64=makeQuery(id+"F6.imprint","IMPRINT",FACE,{"disambiguationData":[TD([[makeQuery(id+"F6.imprint","IMPRINT",EDGE,{"derivedFrom":subQ0}),1.0]])]});}
            extrude(context, id + "F7", {"entities" : qUnion([Q0, Q1, Q2, Q3, Q4, Q5, Q6, Q7, Q8, Q9, Q10, Q11, Q12, Q13, Q14, Q15, Q16, Q17, Q18, Q19, Q20, Q21, Q22, Q23, Q24, Q25, Q26, Q27, Q28, Q29, Q30, Q31, Q32, Q33, Q34, Q35, Q36, Q37, Q38, Q39, Q40, Q41, Q42, Q43, Q44, Q45, Q46, Q47, Q48, Q49, Q50, Q51, Q52, Q53, Q54, Q55, Q56, Q57, Q58, Q59, Q60, Q61, Q62, Q63, Q64]), "operationType" : NewBodyOperationType.ADD, "depth" : 35.27 * mm});
        }
        {
            var Q0;
            Q0=makeQuery(id+"F3.opExtrude","CAP_FACE",FACE,{"disambiguationData":[OSD([sQuery(id+"F2.wireOp",EDGE,"E7")])],"isStart":false});
            var sketch = newSketch(context, id + "F8", { "sketchPlane" : qUnion([Q0])});
            skCircle(sketch, "E273", {"center": v(16.26, -16) * mm, "radius": 1.27 * mm});
            skSolve(sketch);
        }
        {
            var Q0;
            Q0=makeQuery(id+"F3.opExtrude","CAP_FACE",FACE,{"disambiguationData":[OSD([sQuery(id+"F2.wireOp",EDGE,"E10")])],"isStart":false});
            var sketch = newSketch(context, id + "F9", { "sketchPlane" : qUnion([Q0])});
            skCircle(sketch, "E274", {"center": v(48, -16) * mm, "radius": 1.27 * mm});
            skSolve(sketch);
        }
        {
            var Q0;
            Q0=makeQuery(id+"F3.opExtrude","CAP_FACE",FACE,{"disambiguationData":[OSD([sQuery(id+"F2.wireOp",EDGE,"E11")])],"isStart":false});
            var sketch = newSketch(context, id + "F10", { "sketchPlane" : qUnion([Q0])});
            skCircle(sketch, "E275", {"center": v(110.74, -16) * mm, "radius": 1.27 * mm});
            skSolve(sketch);
        }
        {
            var Q0;
            Q0=makeQuery(id+"F3.opExtrude","CAP_FACE",FACE,{"disambiguationData":[OSD([sQuery(id+"F2.wireOp",EDGE,"E6")])],"isStart":false});
            var sketch = newSketch(context, id + "F11", { "sketchPlane" : qUnion([Q0])});
            skCircle(sketch, "E276", {"center": v(16.26, -47.5) * mm, "radius": 1.27 * mm});
            skSolve(sketch);
        }
        {
            var Q0;
            Q0=makeQuery(id+"F3.opExtrude","CAP_FACE",FACE,{"disambiguationData":[OSD([sQuery(id+"F2.wireOp",EDGE,"E9")])],"isStart":false});
            var sketch = newSketch(context, id + "F12", { "sketchPlane" : qUnion([Q0])});
            skCircle(sketch, "E277", {"center": v(48, -47.5) * mm, "radius": 1.27 * mm});
            skSolve(sketch);
        }
        {
            var Q0;
            Q0=makeQuery(id+"F3.opExtrude","CAP_FACE",FACE,{"disambiguationData":[OSD([sQuery(id+"F2.wireOp",EDGE,"E13")])],"isStart":false});
            var sketch = newSketch(context, id + "F13", { "sketchPlane" : qUnion([Q0])});
            skCircle(sketch, "E278", {"center": v(79, -47.5) * mm, "radius": 1.27 * mm});
            skSolve(sketch);
        }
        {
            var Q0;
            Q0=makeQuery(id+"F3.opExtrude","CAP_FACE",FACE,{"disambiguationData":[OSD([sQuery(id+"F2.wireOp",EDGE,"E14")])],"isStart":false});
            var sketch = newSketch(context, id + "F14", { "sketchPlane" : qUnion([Q0])});
            skCircle(sketch, "E279", {"center": v(110.74, -47.5) * mm, "radius": 1.27 * mm});
            skSolve(sketch);
        }
        {
            var Q0;
            Q0=makeQuery(id+"F3.opExtrude","CAP_FACE",FACE,{"disambiguationData":[OSD([sQuery(id+"F2.wireOp",EDGE,"E12")])],"isStart":false});
            var sketch = newSketch(context, id + "F15", { "sketchPlane" : qUnion([Q0])});
            skCircle(sketch, "E280", {"center": v(79, -16) * mm, "radius": 1.27 * mm});
            skSolve(sketch);
        }
        {
            var Q0;
            Q0=makeQuery(id+"F8.imprint","IMPRINT",FACE,{"disambiguationData":[TD([[makeQuery(id+"F8.imprint","IMPRINT",EDGE,{"derivedFrom":sQuery(id+"F8.wireOp",EDGE,"E273")}),1.0]])]});
            var Q1;
            Q1=makeQuery(id+"F9.imprint","IMPRINT",FACE,{"disambiguationData":[TD([[makeQuery(id+"F9.imprint","IMPRINT",EDGE,{"derivedFrom":sQuery(id+"F9.wireOp",EDGE,"E274")}),1.0]])]});
            var Q2;
            Q2=makeQuery(id+"F15.imprint","IMPRINT",FACE,{"disambiguationData":[TD([[makeQuery(id+"F15.imprint","IMPRINT",EDGE,{"derivedFrom":sQuery(id+"F15.wireOp",EDGE,"E280")}),1.0]])]});
            var Q3;
            Q3=makeQuery(id+"F10.imprint","IMPRINT",FACE,{"disambiguationData":[TD([[makeQuery(id+"F10.imprint","IMPRINT",EDGE,{"derivedFrom":sQuery(id+"F10.wireOp",EDGE,"E275")}),1.0]])]});
            var Q4;
            Q4=makeQuery(id+"F11.imprint","IMPRINT",FACE,{"disambiguationData":[TD([[makeQuery(id+"F11.imprint","IMPRINT",EDGE,{"derivedFrom":sQuery(id+"F11.wireOp",EDGE,"E276")}),1.0]])]});
            var Q5;
            Q5=makeQuery(id+"F12.imprint","IMPRINT",FACE,{"disambiguationData":[TD([[makeQuery(id+"F12.imprint","IMPRINT",EDGE,{"derivedFrom":sQuery(id+"F12.wireOp",EDGE,"E277")}),1.0]])]});
            var Q6;
            Q6=makeQuery(id+"F13.imprint","IMPRINT",FACE,{"disambiguationData":[TD([[makeQuery(id+"F13.imprint","IMPRINT",EDGE,{"derivedFrom":sQuery(id+"F13.wireOp",EDGE,"E278")}),1.0]])]});
            var Q7;
            Q7=makeQuery(id+"F14.imprint","IMPRINT",FACE,{"disambiguationData":[TD([[makeQuery(id+"F14.imprint","IMPRINT",EDGE,{"derivedFrom":sQuery(id+"F14.wireOp",EDGE,"E279")}),1.0]])]});
            extrude(context, id + "F16", {"entities" : qUnion([Q0, Q1, Q2, Q3, Q4, Q5, Q6, Q7]), "operationType" : NewBodyOperationType.REMOVE, "oppositeDirection" : true, "depth" : 0.5 * mm, "hasDraft" : true, "draftAngle" : 50 * degree, "draftPullDirection" : true});
        }
    });
